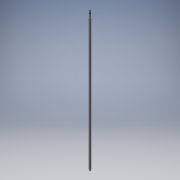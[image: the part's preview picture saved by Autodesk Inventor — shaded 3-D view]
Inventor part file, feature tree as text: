
AUTODESK INVENTOR PART (.ipt)
format: ipt  version: 2018 (Build 220112000, 112)  size: 122,368 bytes
history: native  units: mm
features: extrude x6, sketch x6, other x1, thread x1, chamfer x1
ambient origin geometry x8: Origin, YZ Plane, XZ Plane, XY Plane, X Axis, Y Axis, Z Axis, Center Point
bodies: Body1 (feature_tree)
feature tree (15):
  other  "Sólido1"
  extrude  "Extrusão1"  Depth=1014.5mm TaperAngle=0.0deg
  extrude  "Extrusão2"  Depth=39.0mm TaperAngle=0.0deg
  extrude  "Extrusão3"  Depth=15.0mm TaperAngle=0.0deg
  extrude  "Extrusão4"  Depth=9.15mm TaperAngle=0.0deg
  extrude  "Extrusão5"  Depth=1.15mm TaperAngle=0.0deg
  extrude  "Extrusão6"  Depth=1.85mm TaperAngle=0.0deg
  thread  "Rosca1"  [1 undecoded]
  chamfer  "Chanfro1"  Distance=0.5mm Angle=45.0deg
  sketch  "Esboço1"  dims[d0=16.0mm d1=1014.5mm d2=0.0mm]
  sketch  "Esboço2"  dims[d3=12.0mm d4=39.0mm d5=0.0mm]
  sketch  "Esboço3"  dims[d6=10.0mm d7=15.0mm d8=0.0mm]
  sketch  "Esboço4"  dims[d9=10.0mm d10=9.15mm d11=0.0mm]
  sketch  "Esboço5"  dims[d12=9.0mm d13=1.15mm d14=0.0mm]
  sketch  "Esboço6"  dims[d15=10.0mm d16=1.85mm d17=0.0mm d18=14.0mm d19=0.0mm d20=0.5mm d21=2.0mm d22=45.0deg]
note: 1 required parameter value undecoded (feature->parameter linkage not recoverable at this tier; creation-order binding heuristic only, values carry confidence <= 0.55)
